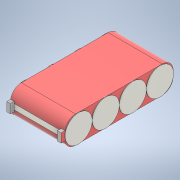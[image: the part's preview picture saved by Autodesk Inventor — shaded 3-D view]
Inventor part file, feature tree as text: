
AUTODESK INVENTOR PART (.ipt)
format: ipt  version: 2022 (Build 260153000, 153)  size: 253,952 bytes
history: native  units: mm
features: extrude x3, sketch x3, fillet x1, plane x1, mirror x1
ambient origin geometry x8: Origin, YZ Plane, XZ Plane, XY Plane, X Axis, Y Axis, Z Axis, Center Point
bodies: Solid1 (feature_tree)
feature tree (9):
  extrude  "Extrusion1"  Depth=60.0mm
  extrude  "Extrusion2"  Depth=15.0mm
  fillet  "Fillet1"  Radius=15.0mm
  extrude  "Extrusion3"  Depth=5.0mm
  plane  "Work Plane1"
  mirror  "Mirror1"
  sketch  "Sketch1"  dims[d0=30.0mm d1=60.0mm]
  sketch  "Sketch2"  dims[d2=30.0mm d3=15.0mm d4=15.0mm d5=0.0mm]
  sketch  "Sketch3"  dims[d6=2.0mm d7=5.0mm d8=5.0mm d9=2.0mm d10=5.0mm d11=5.0mm d12=2.0mm d13=0.0mm d14=6.0mm d15=15.0mm d16=15.0mm d17=15.0mm d18=15.0mm d19=7.5mm d20=0.25mm d21=0.0mm]
